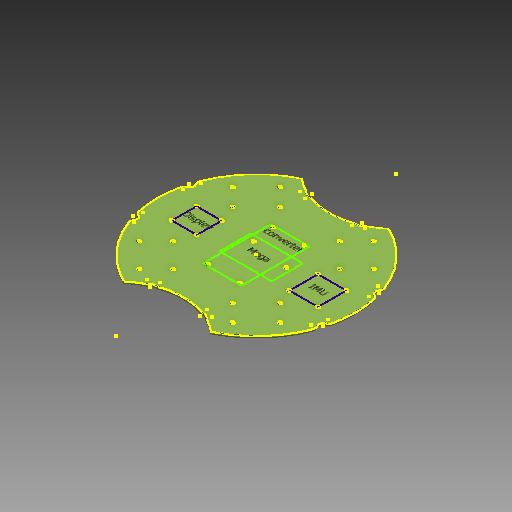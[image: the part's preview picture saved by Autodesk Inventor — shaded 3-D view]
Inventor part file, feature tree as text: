
AUTODESK INVENTOR PART (.ipt)
format: ipt  version: 2020 (Build 240168000, 168)  size: 322,048 bytes
history: native  units: mm
features: sketch x8, other x4, hole x4, extrude x2, fillet x1, projected_geometry x1
ambient origin geometry x8: Origin, YZ Plane, XZ Plane, XY Plane, X Axis, Y Axis, Z Axis, Center Point
bodies: Body1 (feature_tree)
feature tree (20):
  other  "motherboard"
  other  "contour"
  other  "Твердое тело1"
  extrude  "Выдавливание1"  Depth=10.0mm
  hole  "Отверстие1"  [1 undecoded]
  fillet  "Сопряжение1"  Radius=2.0mm
  hole  "Отверстие2"  [1 undecoded]
  sketch  "Эскиз7"
  extrude  "Выдавливание2"  Depth=62.0mm
  hole  "Отверстие3"  [1 undecoded]
  hole  "Отверстие4"  [1 undecoded]
  sketch  "Эскиз10"
  sketch  "Эскиз1"
  sketch  "Эскиз2"
  sketch  "Эскиз3"
  other  "Эскиз3_1"
  sketch  "Эскиз5"
  sketch  "Эскиз8"
  sketch  "Эскиз9"
  projected_geometry  "Спроецированная петля1"
note: 4 required parameter values undecoded (feature->parameter linkage not recoverable at this tier; creation-order binding heuristic only, values carry confidence <= 0.55)
